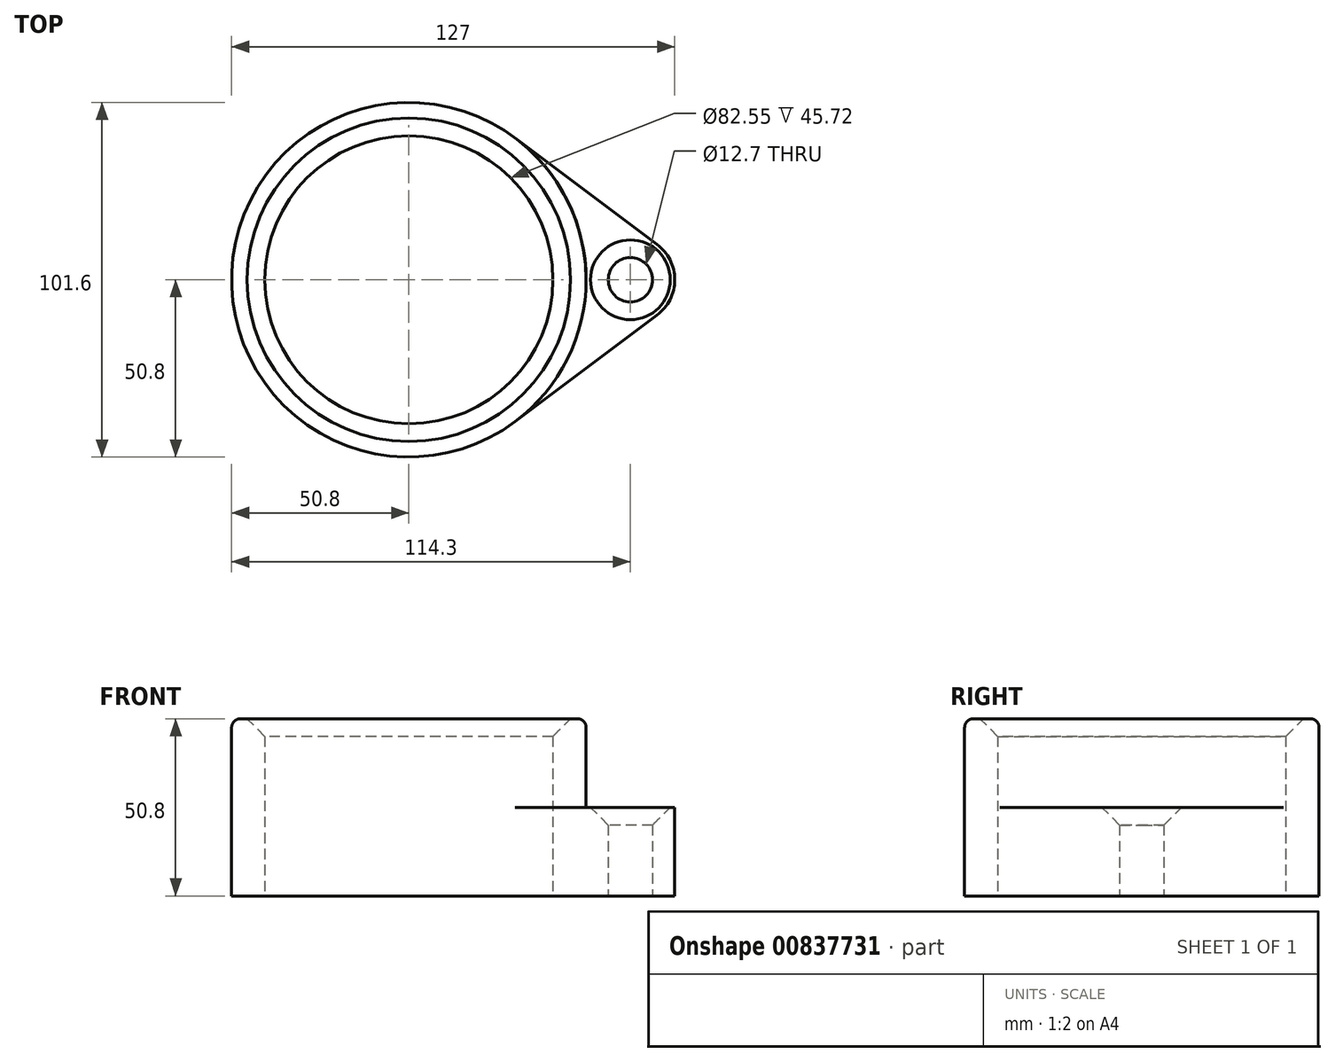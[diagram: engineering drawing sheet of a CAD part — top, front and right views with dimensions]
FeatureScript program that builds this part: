
annotation { "Feature Type Name" : "Feature", "Feature Type Description" : "" }
export const myFeature = defineFeature(function(context is Context, id is Id, definition is map)
    precondition{}
    {
        {
            var Q0;
            Q0=qCreatedBy(makeId("Top.planeOp"),FACE);
            var sketch = newSketch(context, id + "F0", { "sketchPlane" : qUnion([Q0])});
            skCircle(sketch, "E0", {"center": v(0, 0) * mm, "radius": 50.8 * mm});
            skCircle(sketch, "E1", {"center": v(63.5, 0) * mm, "radius": 12.7 * mm});
            skCircle(sketch, "E2", {"center": v(0, 0) * mm, "radius": 41.28 * mm});
            skCircle(sketch, "E3", {"center": v(63.5, 0) * mm, "radius": 6.35 * mm});
            skLineSegment(sketch, "E4", {"start": v(30.48, -40.64) * mm, "end": v(71.12, -10.16) * mm});
            skLineSegment(sketch, "E5", {"start": v(30.48, 40.64) * mm, "end": v(71.12, 10.16) * mm});
            skSolve(sketch);
        }
        {
            var Q0;
            Q0=makeQuery(id+"F0.imprint","IMPRINT",FACE,{"disambiguationData":[TD([[makeQuery(id+"F0.imprint","IMPRINT",EDGE,{"derivedFrom":sQuery(id+"F0.wireOp",EDGE,"E2")}),-1.0]])]});
            var Q1;
            {var subQ0=sQuery(id+"F0.wireOp",EDGE,"biFanbWS-Pbes-MBw5-tZu3-oLHrEFFH4wcL");Q1=makeQuery(id+"F0.imprint","IMPRINT",FACE,{"disambiguationData":[TD([[makeQuery(id+"F0.imprint","IMPRINT",EDGE,{"derivedFrom":subQ0}),1.0]])]});}
            var Q2;
            Q2=makeQuery(id+"F0.imprint","IMPRINT",FACE,{"disambiguationData":[TD([[makeQuery(id+"F0.imprint","IMPRINT",EDGE,{"derivedFrom":sQuery(id+"F0.wireOp",EDGE,"E3")}),-1.0]])]});
            var Q3;
            {var subQ0=sQuery(id+"F0.wireOp",EDGE,"E4");Q3=makeQuery(id+"F0.imprint","IMPRINT",FACE,{"disambiguationData":[TD([[makeQuery(id+"F0.imprint","IMPRINT",EDGE,{"derivedFrom":subQ0}),1.0]])]});}
            var Q4;
            {var subQ0=sQuery(id+"F0.wireOp",EDGE,"E5");Q4=makeQuery(id+"F0.imprint","IMPRINT",FACE,{"disambiguationData":[TD([[makeQuery(id+"F0.imprint","IMPRINT",EDGE,{"derivedFrom":subQ0}),-1.0]])]});}
            extrude(context, id + "F1", {"entities" : qUnion([Q0, Q1, Q2, Q3, Q4]), "depth" : 25.4 * mm, "offsetDistance" : 25.4 * mm});
        }
        {
            var Q0;
            Q0=makeQuery(id+"F0.imprint","IMPRINT",FACE,{"disambiguationData":[TD([[makeQuery(id+"F0.imprint","IMPRINT",EDGE,{"derivedFrom":sQuery(id+"F0.wireOp",EDGE,"E2")}),-1.0]])]});
            extrude(context, id + "F2", {"entities" : qUnion([Q0]), "operationType" : NewBodyOperationType.ADD, "depth" : 50.8 * mm, "offsetDistance" : 25.4 * mm});
        }
        {
            var Q0;
            Q0=makeQuery(id+"F2.opExtrude","CAP_EDGE",EDGE,{"disambiguationData":[OSD([sQuery(id+"F0.wireOp",EDGE,"E0")])],"isStart":false});
            var Q1;
            Q1=makeQuery(id+"F1.opExtrude","CAP_EDGE",EDGE,{"disambiguationData":[OSD([sQuery(id+"F0.wireOp",EDGE,"biFanbWS-Pbes-MBw5-tZu3-oLHrEFFH4wcL")])],"isStart":false});
            fillet(context, id + "F3", {"entities" : qUnion([Q0, Q1]), "radius" : 2.54 * mm, "tangentPropagation" : true, "allowEdgeOverflow" : false});
        }
        {
            var Q0;
            Q0=makeQuery(id+"F2.opExtrude","CAP_EDGE",EDGE,{"disambiguationData":[OSD([sQuery(id+"F0.wireOp",EDGE,"E2")])],"isStart":false});
            var Q1;
            Q1=makeQuery(id+"F1.opExtrude","CAP_EDGE",EDGE,{"disambiguationData":[OSD([sQuery(id+"F0.wireOp",EDGE,"E3")])],"isStart":false});
            chamfer(context, id + "F4", {"entities" : qUnion([Q0, Q1]), "width" : 5.08 * mm, "tangentPropagation" : true});
        }
    });
